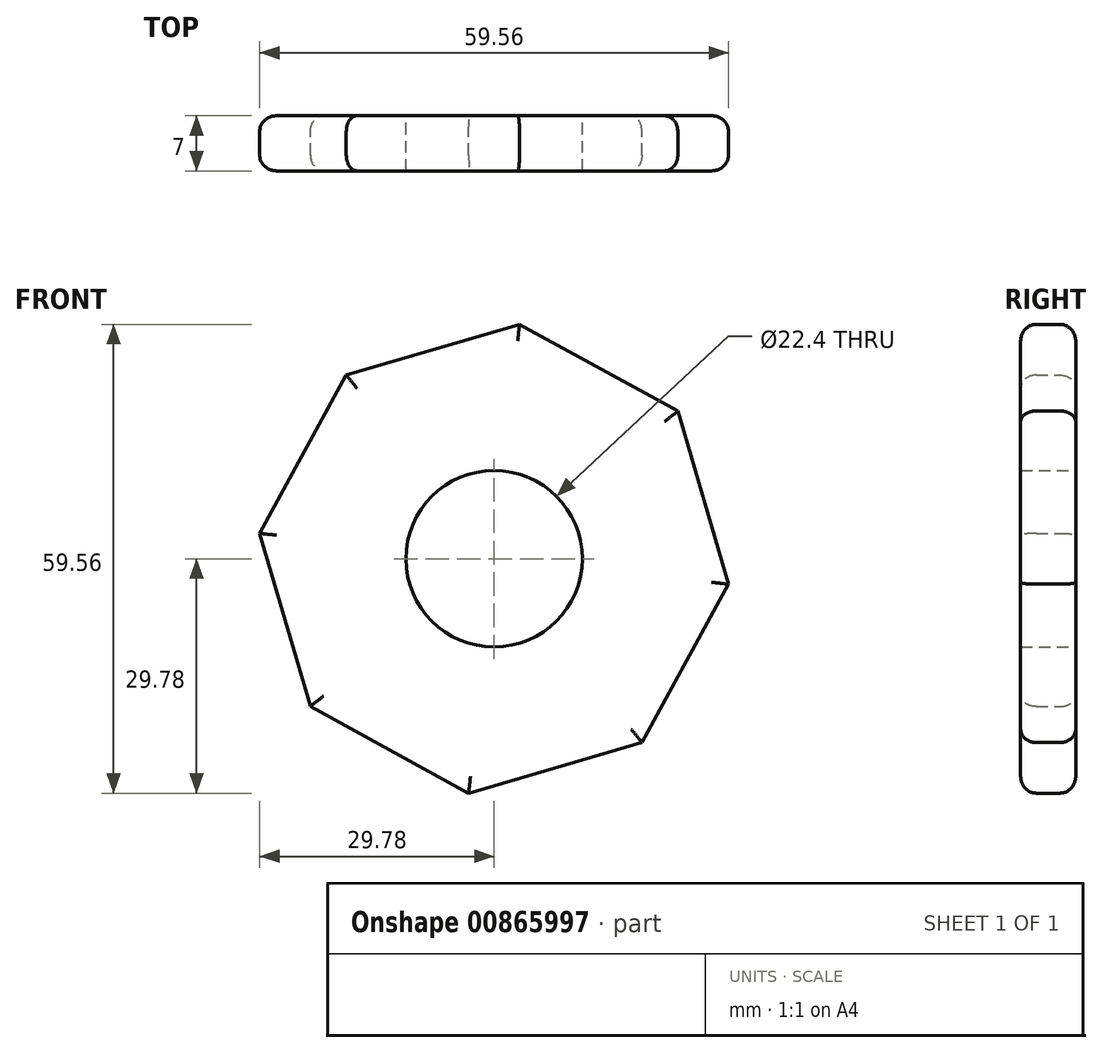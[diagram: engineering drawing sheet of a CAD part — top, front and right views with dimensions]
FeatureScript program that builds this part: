
annotation { "Feature Type Name" : "Feature", "Feature Type Description" : "" }
export const myFeature = defineFeature(function(context is Context, id is Id, definition is map)
    precondition{}
    {
        {
            var Q0;
            Q0=qCreatedBy(makeId("Front.planeOp"),FACE);
            var sketch = newSketch(context, id + "F0", { "sketchPlane" : qUnion([Q0])});
            skCircle(sketch, "E0", {"center": v(0, 0) * mm, "radius": 11.2 * mm});
            skCircle(sketch, "E1", {"center": v(0, 0) * mm, "radius": 13.2 * mm});
            skCircle(sketch, "E2.cCircle", {"center": v(0, 0) * mm, "radius": 27.67 * mm, "construction": true});
            skLineSegment(sketch, "E2.0", {"start": v(29.78, -3.23) * mm, "end": v(18.78, -23.34) * mm});
            skLineSegment(sketch, "E2.1", {"start": v(18.78, -23.34) * mm, "end": v(-3.23, -29.78) * mm});
            skLineSegment(sketch, "E2.2", {"start": v(-3.23, -29.78) * mm, "end": v(-23.34, -18.78) * mm});
            skLineSegment(sketch, "E2.3", {"start": v(-23.34, -18.78) * mm, "end": v(-29.78, 3.23) * mm});
            skLineSegment(sketch, "E2.4", {"start": v(-29.78, 3.23) * mm, "end": v(-18.78, 23.34) * mm});
            skLineSegment(sketch, "E2.5", {"start": v(-18.78, 23.34) * mm, "end": v(3.23, 29.78) * mm});
            skLineSegment(sketch, "E2.6", {"start": v(3.23, 29.78) * mm, "end": v(23.34, 18.78) * mm});
            skLineSegment(sketch, "E2.7", {"start": v(23.34, 18.78) * mm, "end": v(29.78, -3.23) * mm});
            skPoint(sketch, "E2.0.midPoint", {"position": v(24.28, -13.28) * mm});
            skSolve(sketch);
        }
        {
            var Q0;
            Q0=makeQuery(id+"F0.imprint","IMPRINT",FACE,{"disambiguationData":[TD([[makeQuery(id+"F0.imprint","IMPRINT",EDGE,{"derivedFrom":sQuery(id+"F0.wireOp",EDGE,"E1")}),-1.0]])]});
            var Q1;
            Q1=makeQuery(id+"F0.imprint","IMPRINT",FACE,{"disambiguationData":[TD([[makeQuery(id+"F0.imprint","IMPRINT",EDGE,{"derivedFrom":sQuery(id+"F0.wireOp",EDGE,"E0")}),-1.0]])]});
            extrude(context, id + "F1", {"entities" : qUnion([Q0, Q1]), "depth" : 7 * mm, "offsetDistance" : 25 * mm});
        }
        {
            var Q0;
            Q0=makeQuery(id+"F1.opExtrude","CAP_EDGE",EDGE,{"disambiguationData":[OSD([sQuery(id+"F0.wireOp",EDGE,"E2.6")])],"isStart":true});
            var Q1;
            Q1=makeQuery(id+"F1.opExtrude","CAP_EDGE",EDGE,{"disambiguationData":[OSD([sQuery(id+"F0.wireOp",EDGE,"E2.7")])],"isStart":true});
            var Q2;
            Q2=makeQuery(id+"F1.opExtrude","CAP_EDGE",EDGE,{"disambiguationData":[OSD([sQuery(id+"F0.wireOp",EDGE,"E2.0")])],"isStart":true});
            var Q3;
            Q3=makeQuery(id+"F1.opExtrude","CAP_EDGE",EDGE,{"disambiguationData":[OSD([sQuery(id+"F0.wireOp",EDGE,"E2.1")])],"isStart":true});
            var Q4;
            Q4=makeQuery(id+"F1.opExtrude","CAP_EDGE",EDGE,{"disambiguationData":[OSD([sQuery(id+"F0.wireOp",EDGE,"E2.2")])],"isStart":true});
            var Q5;
            Q5=makeQuery(id+"F1.opExtrude","CAP_EDGE",EDGE,{"disambiguationData":[OSD([sQuery(id+"F0.wireOp",EDGE,"E2.3")])],"isStart":true});
            var Q6;
            Q6=makeQuery(id+"F1.opExtrude","CAP_EDGE",EDGE,{"disambiguationData":[OSD([sQuery(id+"F0.wireOp",EDGE,"E2.4")])],"isStart":true});
            var Q7;
            Q7=makeQuery(id+"F1.opExtrude","CAP_EDGE",EDGE,{"disambiguationData":[OSD([sQuery(id+"F0.wireOp",EDGE,"E2.5")])],"isStart":true});
            fillet(context, id + "F2", {"entities" : qUnion([Q0, Q1, Q2, Q3, Q4, Q5, Q6, Q7]), "radius" : 2 * mm, "tangentPropagation" : true, "allowEdgeOverflow" : false});
        }
        {
            var Q0;
            Q0=makeQuery(id+"F1.opExtrude","CAP_EDGE",EDGE,{"disambiguationData":[OSD([sQuery(id+"F0.wireOp",EDGE,"E2.5")])],"isStart":false});
            var Q1;
            Q1=makeQuery(id+"F1.opExtrude","CAP_EDGE",EDGE,{"disambiguationData":[OSD([sQuery(id+"F0.wireOp",EDGE,"E2.4")])],"isStart":false});
            var Q2;
            Q2=makeQuery(id+"F1.opExtrude","CAP_EDGE",EDGE,{"disambiguationData":[OSD([sQuery(id+"F0.wireOp",EDGE,"E2.3")])],"isStart":false});
            var Q3;
            Q3=makeQuery(id+"F1.opExtrude","CAP_EDGE",EDGE,{"disambiguationData":[OSD([sQuery(id+"F0.wireOp",EDGE,"E2.2")])],"isStart":false});
            var Q4;
            Q4=makeQuery(id+"F1.opExtrude","CAP_EDGE",EDGE,{"disambiguationData":[OSD([sQuery(id+"F0.wireOp",EDGE,"E2.1")])],"isStart":false});
            var Q5;
            Q5=makeQuery(id+"F1.opExtrude","CAP_EDGE",EDGE,{"disambiguationData":[OSD([sQuery(id+"F0.wireOp",EDGE,"E2.0")])],"isStart":false});
            var Q6;
            Q6=makeQuery(id+"F1.opExtrude","CAP_EDGE",EDGE,{"disambiguationData":[OSD([sQuery(id+"F0.wireOp",EDGE,"E2.7")])],"isStart":false});
            var Q7;
            Q7=makeQuery(id+"F1.opExtrude","CAP_EDGE",EDGE,{"disambiguationData":[OSD([sQuery(id+"F0.wireOp",EDGE,"E2.6")])],"isStart":false});
            fillet(context, id + "F3", {"entities" : qUnion([Q0, Q1, Q2, Q3, Q4, Q5, Q6, Q7]), "radius" : 2 * mm, "tangentPropagation" : true, "allowEdgeOverflow" : false});
        }
    });
